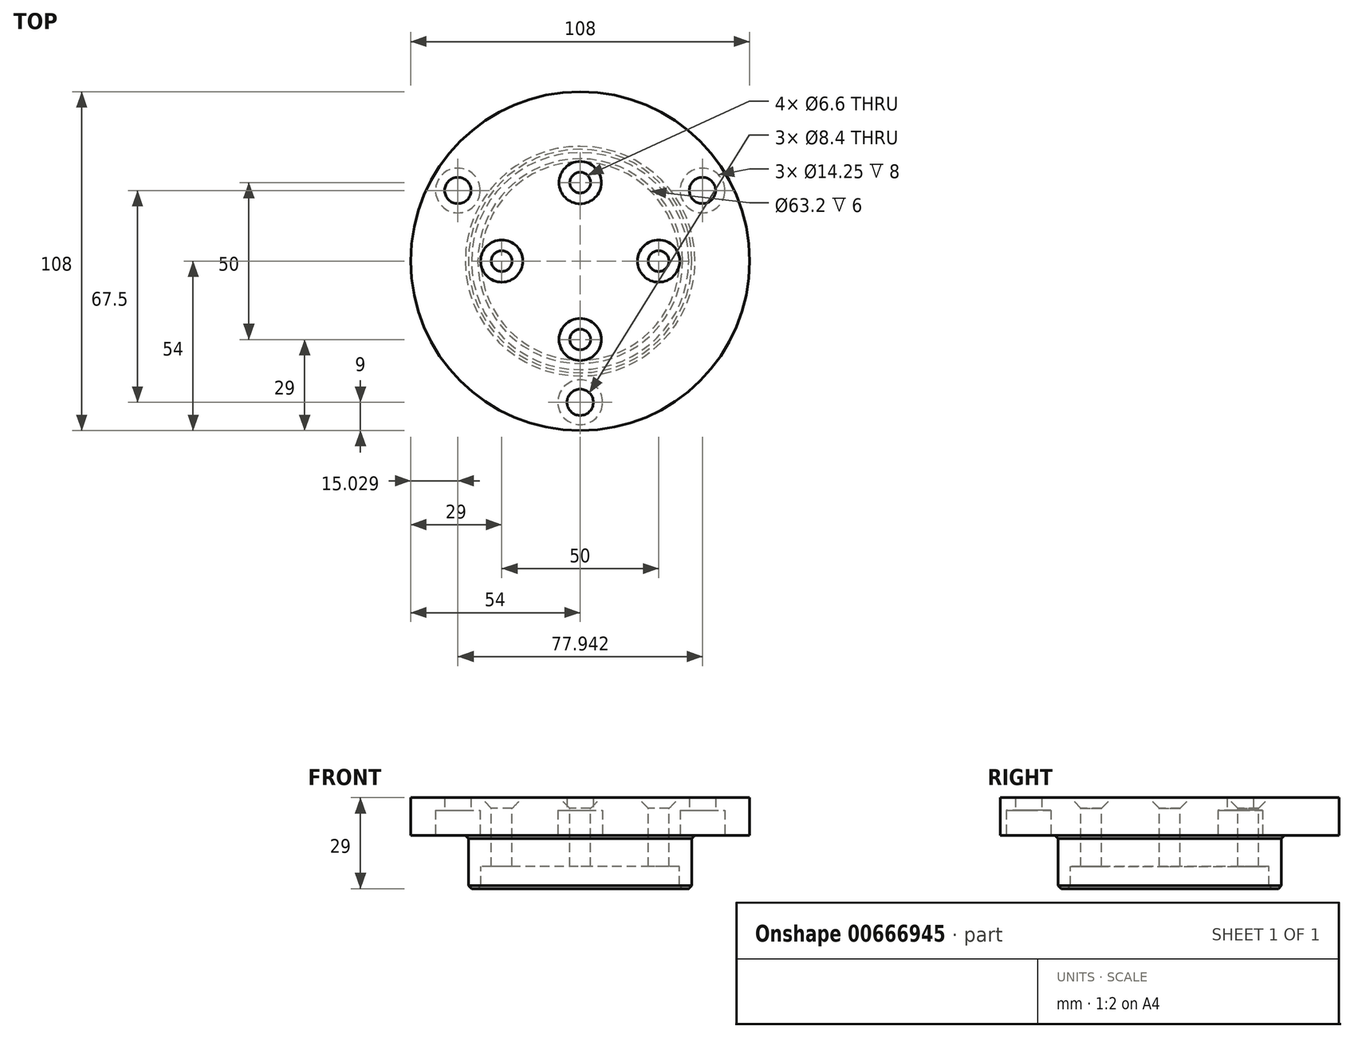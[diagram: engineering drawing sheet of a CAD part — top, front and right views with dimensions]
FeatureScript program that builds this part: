
annotation { "Feature Type Name" : "Feature", "Feature Type Description" : "" }
export const myFeature = defineFeature(function(context is Context, id is Id, definition is map)
    precondition{}
    {
        {
            var Q0;
            Q0=qCreatedBy(makeId("Front.planeOp"),FACE);
            var sketch = newSketch(context, id + "F0", { "sketchPlane" : qUnion([Q0])});
            skLineSegment(sketch, "E0", {"start": v(0, 0) * mm, "end": v(31.6, 0) * mm});
            skLineSegment(sketch, "E1", {"start": v(31.6, 0) * mm, "end": v(31.6, -7) * mm});
            skLineSegment(sketch, "E2", {"start": v(31.6, -7) * mm, "end": v(35.6, -7) * mm});
            skLineSegment(sketch, "E3", {"start": v(35.6, -7) * mm, "end": v(35.6, 10) * mm});
            skLineSegment(sketch, "E4", {"start": v(35.6, 10) * mm, "end": v(0, 10) * mm});
            skLineSegment(sketch, "E5", {"start": v(0, 10) * mm, "end": v(0, 0) * mm});
            skLineSegment(sketch, "E6", {"start": v(35.6, 10) * mm, "end": v(54, 10) * mm});
            skLineSegment(sketch, "E7", {"start": v(54, 10) * mm, "end": v(54, 22) * mm});
            skLineSegment(sketch, "E8", {"start": v(54, 22) * mm, "end": v(0, 22) * mm});
            skLineSegment(sketch, "E9", {"start": v(0, 22) * mm, "end": v(0, 10) * mm});
            skSolve(sketch);
        }
        {
            var Q0;
            Q0=qSketchRegion(id+"F0",true);
            var Q1;
            Q1=sQuery(id+"F0.wireOp",EDGE,"E5");
            revolve(context, id + "F1", {"entities" : qUnion([Q0]), "axis" : qUnion([Q1]), "revolveType" : RevolveType.FULL});
        }
        {
            var Q0;
            Q0=makeQuery(id+"F1.opRevolve","SWEPT_EDGE",EDGE,{"disambiguationData":[OSD([sQuery(id+"F0.wireOp",EDGE,"E1"),sQuery(id+"F0.wireOp",EDGE,"E2")])]});
            var Q1;
            Q1=makeQuery(id+"F1.opRevolve","SWEPT_EDGE",EDGE,{"disambiguationData":[OSD([sQuery(id+"F0.wireOp",EDGE,"E2"),sQuery(id+"F0.wireOp",EDGE,"E3")])]});
            var Q2;
            Q2=makeQuery(id+"F1.opRevolve","SWEPT_EDGE",EDGE,{"disambiguationData":[OSD([sQuery(id+"F0.wireOp",EDGE,"E3"),sQuery(id+"F0.wireOp",EDGE,"E4")])]});
            chamfer(context, id + "F2", {"entities" : qUnion([Q0, Q1, Q2]), "width" : 1 * mm, "tangentPropagation" : true});
        }
        {
            var Q0;
            Q0=makeQuery(id+"F1.opRevolve","SWEPT_FACE",FACE,{"disambiguationData":[OSD([sQuery(id+"F0.wireOp",EDGE,"E8")])]});
            var sketch = newSketch(context, id + "F3", { "sketchPlane" : qUnion([Q0])});
            skCircle(sketch, "E10", {"center": v(0, 0) * mm, "radius": 25 * mm, "construction": true});
            skPoint(sketch, "E11", {"position": v(-25, 0) * mm});
            skPoint(sketch, "E12", {"position": v(25, 0) * mm});
            skPoint(sketch, "E13", {"position": v(0, 25) * mm});
            skPoint(sketch, "E14", {"position": v(0, -25) * mm});
            skSolve(sketch);
        }
        {
            var Q0;
            Q0=sQuery(id+"F3.wireOp",VERTEX,"E11");
            var Q1;
            Q1=sQuery(id+"F3.wireOp",VERTEX,"E12");
            var Q2;
            Q2=sQuery(id+"F3.wireOp",VERTEX,"E14");
            var Q3;
            Q3=sQuery(id+"F3.wireOp",VERTEX,"E13");
            var Q4;
            Q4=makeQuery(id+"F1.opRevolve","SWEPT_BODY",BODY,{"disambiguationData":[OSD([sQuery(id+"F0.wireOp",EDGE,"E0"),sQuery(id+"F0.wireOp",EDGE,"E1"),sQuery(id+"F0.wireOp",EDGE,"E2"),sQuery(id+"F0.wireOp",EDGE,"E3"),sQuery(id+"F0.wireOp",EDGE,"E4"),sQuery(id+"F0.wireOp",EDGE,"E5")])]});
            hole(context, id + "F4", {"style" : HoleStyle.C_SINK, "endStyle" : HoleEndStyle.THROUGH, "standardTappedOrClearance" : lookupTablePath({ "standard" : "ISO", "fit" : "Normal", "size" : "M6", "type" : "Clearance" }), "standardBlindInLast" : lookupTablePath({ "fit" : "Standard", "standard" : "ISO", "size" : "M6", "type" : "Clearance" }), "holeDiameter" : 6.6 * mm, "cSinkDiameter" : 13.44 * mm, "cSinkAngle" : 90 * degree, "locations" : qUnion([Q0, Q1, Q2, Q3]), "scope" : qUnion([Q4]), "majorDiameter" : 5 * mm, "tappedDepth" : 12 * mm, "tapClearance" : 3});
        }
        {
            var Q0;
            Q0=makeQuery(id+"F1.opRevolve","SWEPT_FACE",FACE,{"disambiguationData":[OSD([sQuery(id+"F0.wireOp",EDGE,"E6")])]});
            var sketch = newSketch(context, id + "F5", { "sketchPlane" : qUnion([Q0])});
            skCircle(sketch, "E15", {"center": v(0, 0) * mm, "radius": 45 * mm, "construction": true});
            skPoint(sketch, "E16", {"position": v(0, 45) * mm});
            skLineSegment(sketch, "E17", {"start": v(0, 0) * mm, "end": v(0, 45) * mm, "construction": true});
            skLineSegment(sketch, "E18", {"start": v(0, 0) * mm, "end": v(-38.97, -22.5) * mm, "construction": true});
            skLineSegment(sketch, "E19", {"start": v(0, 0) * mm, "end": v(38.97, -22.5) * mm, "construction": true});
            skPoint(sketch, "E20", {"position": v(-38.97, -22.5) * mm});
            skPoint(sketch, "E21", {"position": v(38.97, -22.5) * mm});
            skPoint(sketch, "E22", {"position": v(-45, 0) * mm});
            skPoint(sketch, "E23", {"position": v(45, 0) * mm});
            skSolve(sketch);
        }
        {
            var Q0;
            Q0=sQuery(id+"F5.wireOp",VERTEX,"E20");
            var Q1;
            Q1=sQuery(id+"F5.wireOp",VERTEX,"E21");
            var Q2;
            Q2=sQuery(id+"F5.wireOp",VERTEX,"E16");
            var Q3;
            Q3=makeQuery(id+"F1.opRevolve","SWEPT_BODY",BODY,{"disambiguationData":[OSD([sQuery(id+"F0.wireOp",EDGE,"E0"),sQuery(id+"F0.wireOp",EDGE,"E1"),sQuery(id+"F0.wireOp",EDGE,"E2"),sQuery(id+"F0.wireOp",EDGE,"E3"),sQuery(id+"F0.wireOp",EDGE,"E4"),sQuery(id+"F0.wireOp",EDGE,"E5")])]});
            hole(context, id + "F6", {"style" : HoleStyle.C_BORE, "endStyle" : HoleEndStyle.THROUGH, "standardTappedOrClearance" : lookupTablePath({ "standard" : "ISO", "fit" : "Close", "size" : "M8", "type" : "Clearance" }), "standardBlindInLast" : lookupTablePath({ "fit" : "Close", "standard" : "ISO", "size" : "M8", "type" : "Clearance" }), "holeDiameter" : 8.4 * mm, "cBoreDiameter" : 14.25 * mm, "cBoreDepth" : 8 * mm, "locations" : qUnion([Q0, Q1, Q2]), "scope" : qUnion([Q3]), "majorDiameter" : 5 * mm, "tappedDepth" : 12 * mm, "tapClearance" : 3});
        }
    });
